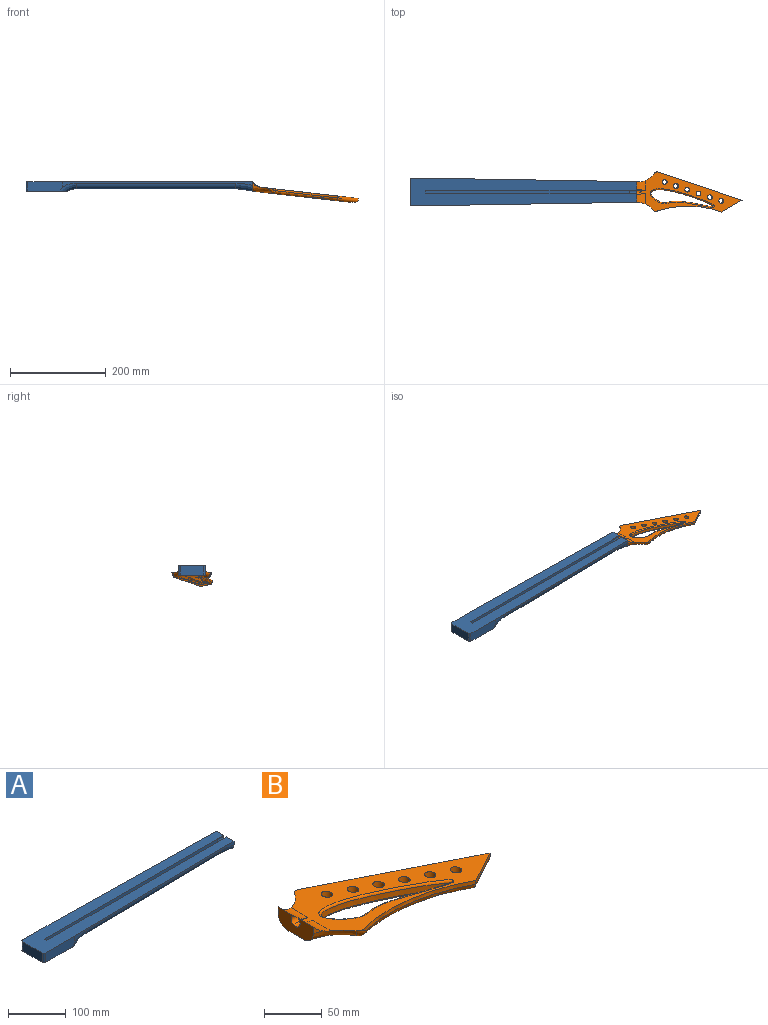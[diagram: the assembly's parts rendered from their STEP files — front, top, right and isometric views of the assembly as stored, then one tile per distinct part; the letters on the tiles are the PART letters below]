
ASSEMBLY  parts=2 mates=1
PART A: 33 faces, bbox 478.2x59.2x29.9 mm
  f0: plane 425x9mm, normal (0,1,0), area 3825mm2, adj f2,f12,f16,f18
  f1: plane 425x9mm, normal (0,-1,0), area 3825mm2, adj f2,f12,f16,f18
  f2: plane 425x6mm, normal (0,0,1), area 2550mm2, adj f0,f1,f16,f18
  f3: plane 43x20mm, normal (1,0,0), area 705.4mm2, adj f8,f9,f12,f15,f17,f21,f24
  f4: plane 88.93x58.93mm, normal (0,0,-1), area 4676mm2, adj f5,f6,f7,f10,f11,f14,f19,f22
  f5: plane 48x20mm, normal (-1,0,0), area 960mm2, adj f4,f6,f11,f12
  f6: cylinder r=4mm len=20mm, axis (0,0,-1), area 125.7mm2, adj f4,f5,f7,f12
  f7: plane 72.76x20.76mm, normal (0,-1,0), area 1417.1mm2, adj f4,f6,f8,f12,f22
  f8: plane 396.35x12.35mm, normal (0.02,-1,0), area 1338.1mm2, adj f3,f7,f12,f22,f23,f24
  f9: plane 396.35x12.35mm, normal (0.02,1,0), area 1338.1mm2, adj f3,f10,f12,f19,f20,f21
  f10: plane 72.76x20.76mm, normal (0,1,0), area 1417.1mm2, adj f4,f9,f11,f12,f19
  f11: cylinder r=4mm len=20mm, axis (0,0,-1), area 125.7mm2, adj f4,f5,f10,f12
  f12: plane 472.35x56mm, normal (0,0,1), area 21223.6mm2, adj f0,f1,f3,f5,f6,f7,f8,f9
  f13: plane 331.98x31.03mm, normal (0,0,-1), area 8495.1mm2, adj f14,f15,f20,f21,f23,f24
  f14: cylinder r=36.6mm len=31.87mm, axis (0,1,0), area 637.3mm2, adj f4,f13,f19,f22
  f15: cylinder r=209mm len=35mm, axis (0,1,0), area 690.8mm2, adj f3,f13,f21,f24
  f16: plane 9x6mm, normal (1,0,0), area 54mm2, adj f0,f1,f2,f12
  f17: cylinder r=5.5mm len=15mm, axis (1,0,0), area 417.3mm2, adj f3,f12,f18
  f18: plane 11x10mm, normal (1,0,0), area 36.7mm2, adj f0,f1,f2,f12,f17
  f19: bspline ~37.19x24.02mm, area 550.3mm2, adj f4,f9,f10,f14,f20
  f20: cylinder r=12mm len=332.52mm, axis (-1,0.02,0), area 6261.8mm2, adj f9,f13,f19,f21
  f21: bspline ~38.22x17mm, area 663.2mm2, adj f3,f9,f13,f15,f20
  f22: bspline ~37.19x24.02mm, area 550.3mm2, adj f4,f7,f8,f14,f23
  f23: cylinder r=12mm len=332.52mm, axis (1,0.02,0), area 6261.8mm2, adj f8,f13,f22,f24
  f24: bspline ~38.22x17mm, area 663.2mm2, adj f3,f8,f13,f15,f23
  f25: cylinder r=1.5mm len=5mm, axis (0,0,-1), area 47.1mm2, adj f4,f26
  f26: plane 3x3mm, normal (0,0,-1), area 7.1mm2, adj f25
  f27: cylinder r=1.5mm len=5mm, axis (0,0,-1), area 47.1mm2, adj f4,f28
  f28: plane 3x3mm, normal (0,0,-1), area 7.1mm2, adj f27
  f29: cylinder r=1.5mm len=5mm, axis (0,0,-1), area 47.1mm2, adj f4,f30
  f30: plane 3x3mm, normal (0,0,-1), area 7.1mm2, adj f29
  f31: cylinder r=1.5mm len=5mm, axis (0,0,-1), area 47.1mm2, adj f4,f32
  f32: plane 3x3mm, normal (0,0,-1), area 7.1mm2, adj f31
PART B: 42 faces, bbox 223.7x86x44.7 mm
  f0: cylinder r=30mm len=22.16mm, axis (0,1,0), area 426.1mm2, adj f1,f5,f6,f11,f21,f23
  f1: plane 43.67x19.67mm, normal (-1,0,0), area 663.2mm2, adj f0,f3,f4,f6,f10,f11,f12,f23
  f2: extruded ~130.08x34.68mm, area 1580.7mm2, adj f18,f19,f20
  f3: plane 204.95x69.39mm, normal (-0.11,0,-0.99), area 4167.7mm2, adj f1,f11,f12,f14,f15,f16,f19,f24
  f4: cylinder r=30mm len=20.53mm, axis (0,1,0), area 406.7mm2, adj f1,f5,f10,f12,f22,f23
  f5: plane 220.15x84.77mm, normal (0.11,0,0.99), area 6544.6mm2, adj f0,f4,f7,f8,f9,f11,f12,f13
  f6: cylinder r=45mm len=10.34mm, axis (0,0,1), area 36.1mm2, adj f0,f1,f11
  f7: cylinder r=200mm len=135.56mm, axis (0,0,1), area 547.1mm2, adj f5,f8,f15,f16,f17
  f8: plane 42.25x25mm, normal (0.51,-0.86,0), area 177.8mm2, adj f5,f7,f9,f15
  f9: plane 175.16x58.39mm, normal (0.32,0.95,0), area 691.4mm2, adj f5,f8,f13,f14,f15
  f10: cylinder r=40mm len=10.03mm, axis (0,0,1), area 34mm2, adj f1,f4,f12
  f11: bspline ~46.12x30.55mm, area 789.5mm2, adj f0,f1,f3,f5,f6,f17
  f12: bspline ~50.02x31.04mm, area 850.5mm2, adj f1,f3,f4,f5,f10,f13
  f13: bspline ~14.14x13.16mm, area 110.8mm2, adj f5,f9,f12,f14
  f14: cylinder r=6mm len=172.66mm, axis (-0.94,0.31,0.11), area 1674.4mm2, adj f3,f9,f13,f15
  f15: cylinder r=6mm len=46.01mm, axis (0.86,0.51,-0.1), area 426.8mm2, adj f3,f7,f8,f9,f14,f16
  f16: bspline ~134.37x21.23mm, area 1018.7mm2, adj f3,f7,f15,f17,f20
  f17: bspline ~12.34x12.21mm, area 106.9mm2, adj f5,f7,f11,f16
  f18: bspline ~134.11x38.82mm, area 894mm2, adj f2,f5
  f19: bspline ~133.51x37.15mm, area 721.3mm2, adj f2,f3,f20
  f20: bspline ~60.53x13.1mm, area 256.2mm2, adj f2,f16,f19
  f21: plane 17.11x1.95mm, normal (0,1,0), area 9.7mm2, adj f0,f5,f23
  f22: plane 15.77x1.8mm, normal (0,-1,0), area 8.1mm2, adj f4,f5,f23
  f23: cylinder r=5.5mm len=12.04mm, axis (-1,0,0), area 170.1mm2, adj f0,f1,f4,f5,f21,f22
  f24: cylinder r=1.2mm len=2.61mm, axis (-0.11,0,-0.99), area 15.1mm2, adj f3,f25
  f25: plane 2.4x2.38mm, normal (-0.11,0,-0.99), area 4.5mm2, adj f24
  f26: cylinder r=5mm len=11.06mm, axis (-0.11,0,-0.99), area 313.7mm2, adj f3,f5
  f27: cylinder r=5mm len=11.06mm, axis (-0.11,0,-0.99), area 313.5mm2, adj f3,f5
  f28: cylinder r=5mm len=11.06mm, axis (-0.11,0,-0.99), area 313.2mm2, adj f3,f5
  f29: cylinder r=1.2mm len=2.61mm, axis (-0.11,0,-0.99), area 15.1mm2, adj f3,f30
  f30: plane 2.4x2.38mm, normal (-0.11,0,-0.99), area 4.5mm2, adj f29
  f31: cylinder r=1.2mm len=2.61mm, axis (-0.11,0,-0.99), area 15.1mm2, adj f3,f32
  f32: plane 2.4x2.38mm, normal (-0.11,0,-0.99), area 4.5mm2, adj f31
  f33: cylinder r=1.2mm len=2.61mm, axis (-0.11,0,-0.99), area 15.1mm2, adj f3,f34
  f34: plane 2.4x2.38mm, normal (-0.11,0,-0.99), area 4.5mm2, adj f33
  f35: cylinder r=1.2mm len=2.61mm, axis (-0.11,0,-0.99), area 15.1mm2, adj f3,f36
  f36: plane 2.4x2.38mm, normal (-0.11,0,-0.99), area 4.5mm2, adj f35
  f37: cylinder r=5mm len=11.06mm, axis (-0.11,0,-0.99), area 313mm2, adj f3,f5
  f38: cylinder r=5mm len=11.06mm, axis (-0.11,0,-0.99), area 312.8mm2, adj f3,f5
  f39: cylinder r=5mm len=11.06mm, axis (-0.11,0,-0.99), area 312.5mm2, adj f3,f5
  f40: cylinder r=1.2mm len=2.61mm, axis (-0.11,0,-0.99), area 15.1mm2, adj f3,f41
  f41: plane 2.4x2.38mm, normal (-0.11,0,-0.99), area 4.5mm2, adj f40
PLACE A t=(-31.14,6.54,-26.63)mm
PLACE B t=(441.21,-14.87,-26.63)mm
MATE fastened B.f1 <-> A.f3  axis (-1,0,0) through (441.21,6.54,-26.63)mm
